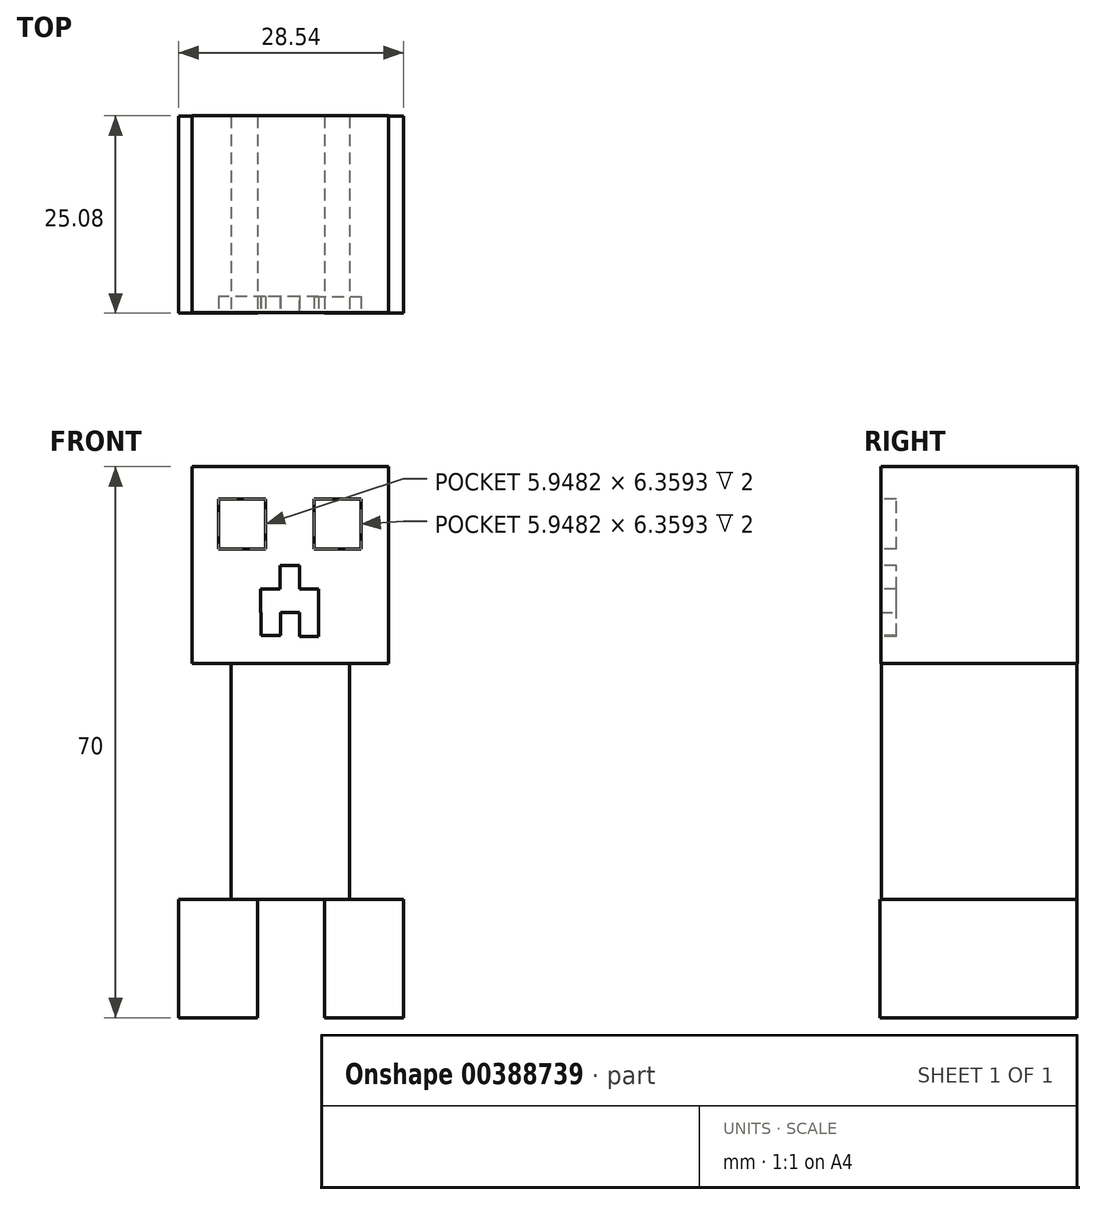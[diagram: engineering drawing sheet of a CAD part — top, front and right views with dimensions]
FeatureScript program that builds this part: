
annotation { "Feature Type Name" : "Feature", "Feature Type Description" : "" }
export const myFeature = defineFeature(function(context is Context, id is Id, definition is map)
    precondition{}
    {
        {
            var Q0;
            Q0=qCreatedBy(makeId("Top.planeOp"),FACE);
            var sketch = newSketch(context, id + "F0", { "sketchPlane" : qUnion([Q0])});
            skLineSegment(sketch, "E0.bottom", {"start": v(-14.1, 14.12) * mm, "end": v(-4.1, 14.12) * mm});
            skLineSegment(sketch, "E0.top", {"start": v(-14.1, -10.88) * mm, "end": v(-4.1, -10.88) * mm});
            skLineSegment(sketch, "E0.left", {"start": v(-14.1, 14.12) * mm, "end": v(-14.1, -10.88) * mm});
            skLineSegment(sketch, "E0.right", {"start": v(-4.1, 14.12) * mm, "end": v(-4.1, -10.88) * mm});
            skLineSegment(sketch, "E1.bottom", {"start": v(4.44, 14.12) * mm, "end": v(14.44, 14.12) * mm});
            skLineSegment(sketch, "E1.top", {"start": v(4.44, -10.88) * mm, "end": v(14.44, -10.88) * mm});
            skLineSegment(sketch, "E1.left", {"start": v(4.44, 14.12) * mm, "end": v(4.44, -10.88) * mm});
            skLineSegment(sketch, "E1.right", {"start": v(14.44, 14.12) * mm, "end": v(14.44, -10.88) * mm});
            skSolve(sketch);
        }
        {
            var Q0;
            Q0=makeQuery(id+"F0.imprint","IMPRINT",FACE,{"disambiguationData":[TD([[makeQuery(id+"F0.imprint","IMPRINT",EDGE,{"derivedFrom":sQuery(id+"F0.wireOp",EDGE,"E0.bottom")}),-1.0]])]});
            var Q1;
            Q1=makeQuery(id+"F0.imprint","IMPRINT",FACE,{"disambiguationData":[TD([[makeQuery(id+"F0.imprint","IMPRINT",EDGE,{"derivedFrom":sQuery(id+"F0.wireOp",EDGE,"E1.bottom")}),-1.0]])]});
            extrude(context, id + "F1", {"entities" : qUnion([Q0, Q1]), "depth" : 15 * mm});
        }
        {
            var Q0;
            Q0=makeQuery(id+"F1.opExtrude","CAP_FACE",FACE,{"disambiguationData":[OSD([sQuery(id+"F0.wireOp",EDGE,"E0.bottom"),sQuery(id+"F0.wireOp",EDGE,"E0.top"),sQuery(id+"F0.wireOp",EDGE,"E0.left"),sQuery(id+"F0.wireOp",EDGE,"E0.right")])],"isStart":false});
            var sketch = newSketch(context, id + "F2", { "sketchPlane" : qUnion([Q0])});
            skLineSegment(sketch, "E2.bottom", {"start": v(-7.42, 14.12) * mm, "end": v(7.58, 14.12) * mm});
            skLineSegment(sketch, "E2.top", {"start": v(-7.42, -10.73) * mm, "end": v(7.58, -10.73) * mm});
            skLineSegment(sketch, "E2.left", {"start": v(-7.42, 14.12) * mm, "end": v(-7.42, -10.73) * mm});
            skLineSegment(sketch, "E2.right", {"start": v(7.58, 14.12) * mm, "end": v(7.58, -10.73) * mm});
            skSolve(sketch);
        }
        {
            var Q0;
            Q0 = qSketchRegion(id + "F2", true);
            extrude(context, id + "F3", {"entities" : qUnion([Q0]), "depth" : 30 * mm});
        }
        {
            var Q0;
            Q0=makeQuery(id+"F3.opExtrude","CAP_FACE",FACE,{"disambiguationData":[OSD([sQuery(id+"F2.wireOp",EDGE,"E2.bottom"),sQuery(id+"F2.wireOp",EDGE,"E2.top"),sQuery(id+"F2.wireOp",EDGE,"E2.left"),sQuery(id+"F2.wireOp",EDGE,"E2.right")])],"isStart":false});
            var sketch = newSketch(context, id + "F4", { "sketchPlane" : qUnion([Q0])});
            skLineSegment(sketch, "E3.bottom", {"start": v(12.58, -10.8) * mm, "end": v(-12.42, -10.8) * mm});
            skLineSegment(sketch, "E3.top", {"start": v(12.58, 14.2) * mm, "end": v(-12.42, 14.2) * mm});
            skLineSegment(sketch, "E3.left", {"start": v(12.58, -10.8) * mm, "end": v(12.58, 14.2) * mm});
            skLineSegment(sketch, "E3.right", {"start": v(-12.42, -10.8) * mm, "end": v(-12.42, 14.2) * mm});
            skPoint(sketch, "E3.middle", {"position": v(0.08, 1.7) * mm});
            skPoint(sketch, "E3.middle.positionSnap0", {"position": v(7.58, 1.7) * mm});
            skPoint(sketch, "E3.middle.positionSnap1", {"position": v(0.08, 14.12) * mm});
            skPoint(sketch, "E3.centerSnap0", {"position": v(7.58, 1.7) * mm});
            skPoint(sketch, "E3.centerSnap1", {"position": v(0.08, 14.12) * mm});
            skSolve(sketch);
        }
        {
            var Q0;
            Q0 = qSketchRegion(id + "F4", true);
            extrude(context, id + "F5", {"entities" : qUnion([Q0]), "operationType" : NewBodyOperationType.ADD, "depth" : 25 * mm});
        }
        {
            var Q0;
            Q0=makeQuery(id+"F5.opExtrude","SWEPT_FACE",FACE,{"disambiguationData":[OSD([sQuery(id+"F4.wireOp",EDGE,"E3.bottom")])]});
            var sketch = newSketch(context, id + "F6", { "sketchPlane" : qUnion([Q0])});
            skLineSegment(sketch, "E4.bottom", {"start": v(-3.1, 59.54) * mm, "end": v(-9.04, 59.54) * mm});
            skLineSegment(sketch, "E4.top", {"start": v(-3.1, 65.9) * mm, "end": v(-9.04, 65.9) * mm});
            skLineSegment(sketch, "E4.left", {"start": v(-3.1, 59.54) * mm, "end": v(-3.1, 65.9) * mm});
            skLineSegment(sketch, "E4.right", {"start": v(-9.04, 59.54) * mm, "end": v(-9.04, 65.9) * mm});
            skPoint(sketch, "E4.middle", {"position": v(-6.07, 62.72) * mm});
            skLineSegment(sketch, "E5.MirrorCS", {"start": v(3.1, 59.54) * mm, "end": v(9.04, 59.54) * mm});
            skPoint(sketch, "E6.MirrorP", {"position": v(6.07, 62.72) * mm});
            skLineSegment(sketch, "E7.MirrorCS", {"start": v(9.04, 59.54) * mm, "end": v(9.04, 65.9) * mm});
            skLineSegment(sketch, "E8.MirrorCS", {"start": v(3.1, 59.54) * mm, "end": v(3.1, 65.9) * mm});
            skLineSegment(sketch, "E9.MirrorCS", {"start": v(3.1, 65.9) * mm, "end": v(9.04, 65.9) * mm});
            skLineSegment(sketch, "E10.bottom", {"start": v(-1.23, 51.5) * mm, "end": v(-3.68, 51.5) * mm});
            skLineSegment(sketch, "E10.top", {"start": v(-1.23, 54.47) * mm, "end": v(-3.68, 54.47) * mm});
            skLineSegment(sketch, "E10.left", {"start": v(-1.23, 51.5) * mm, "end": v(-1.23, 54.47) * mm});
            skLineSegment(sketch, "E10.right", {"start": v(-3.68, 51.5) * mm, "end": v(-3.68, 54.47) * mm});
            skPoint(sketch, "E10.middle", {"position": v(-2.46, 52.98) * mm});
            skLineSegment(sketch, "E11.bottom", {"start": v(1.22, 51.5) * mm, "end": v(-1.23, 51.5) * mm});
            skLineSegment(sketch, "E11.top", {"start": v(1.22, 54.47) * mm, "end": v(-1.23, 54.47) * mm});
            skLineSegment(sketch, "E11.left", {"start": v(1.22, 51.5) * mm, "end": v(1.22, 54.47) * mm});
            skPoint(sketch, "E11.middle", {"position": v(0, 52.98) * mm});
            skLineSegment(sketch, "E12.bottom", {"start": v(3.68, 51.5) * mm, "end": v(1.22, 51.5) * mm});
            skLineSegment(sketch, "E12.top", {"start": v(3.68, 54.47) * mm, "end": v(1.22, 54.47) * mm});
            skLineSegment(sketch, "E12.left", {"start": v(3.68, 51.5) * mm, "end": v(3.68, 54.47) * mm});
            skPoint(sketch, "E12.middle", {"position": v(2.45, 52.98) * mm});
            skLineSegment(sketch, "E13.top", {"start": v(1.22, 57.44) * mm, "end": v(-1.23, 57.44) * mm});
            skLineSegment(sketch, "E13.left", {"start": v(1.22, 54.47) * mm, "end": v(1.22, 57.44) * mm});
            skLineSegment(sketch, "E13.right", {"start": v(-1.23, 54.47) * mm, "end": v(-1.23, 57.44) * mm});
            skPoint(sketch, "E13.middle", {"position": v(0, 55.95) * mm});
            skLineSegment(sketch, "E14.bottom", {"start": v(-1.17, 48.55) * mm, "end": v(-3.62, 48.55) * mm});
            skLineSegment(sketch, "E14.top", {"start": v(-1.17, 51.52) * mm, "end": v(-3.62, 51.52) * mm});
            skLineSegment(sketch, "E14.left", {"start": v(-1.17, 48.55) * mm, "end": v(-1.17, 51.52) * mm});
            skLineSegment(sketch, "E14.right", {"start": v(-3.62, 48.55) * mm, "end": v(-3.62, 51.52) * mm});
            skPoint(sketch, "E14.middle", {"position": v(-2.4, 50.03) * mm});
            skLineSegment(sketch, "E15.bottom", {"start": v(3.55, 48.44) * mm, "end": v(1.25, 48.44) * mm});
            skLineSegment(sketch, "E15.top", {"start": v(3.55, 51.4) * mm, "end": v(1.25, 51.4) * mm});
            skLineSegment(sketch, "E15.left", {"start": v(3.55, 48.44) * mm, "end": v(3.55, 51.4) * mm});
            skLineSegment(sketch, "E15.right", {"start": v(1.25, 48.44) * mm, "end": v(1.25, 51.4) * mm});
            skPoint(sketch, "E15.middle", {"position": v(2.4, 49.92) * mm});
            skSolve(sketch);
        }
        {
            var Q0;
            Q0 = qSketchRegion(id + "F6", true);
            extrude(context, id + "F7", {"entities" : qUnion([Q0]), "operationType" : NewBodyOperationType.REMOVE, "oppositeDirection" : true, "depth" : 2 * mm});
        }
        {
            var Q0;
            Q0=makeQuery(id+"F5.opExtrude","SWEPT_FACE",FACE,{"disambiguationData":[OSD([sQuery(id+"F4.wireOp",EDGE,"E3.bottom")])]});
            var sketch = newSketch(context, id + "F8", { "sketchPlane" : qUnion([Q0])});
            skLineSegment(sketch, "E16.bottom", {"start": v(3.68, 54.47) * mm, "end": v(1.25, 54.47) * mm});
            skLineSegment(sketch, "E16.top", {"start": v(3.68, 48.44) * mm, "end": v(1.25, 48.44) * mm});
            skLineSegment(sketch, "E16.left", {"start": v(3.68, 54.47) * mm, "end": v(3.68, 48.44) * mm});
            skLineSegment(sketch, "E16.right", {"start": v(1.25, 54.47) * mm, "end": v(1.25, 48.44) * mm});
            skSolve(sketch);
        }
        {
            var Q0;
            Q0 = qSketchRegion(id + "F8", true);
            extrude(context, id + "F9", {"entities" : qUnion([Q0]), "operationType" : NewBodyOperationType.REMOVE, "oppositeDirection" : true, "depth" : 2 * mm});
        }
    });
